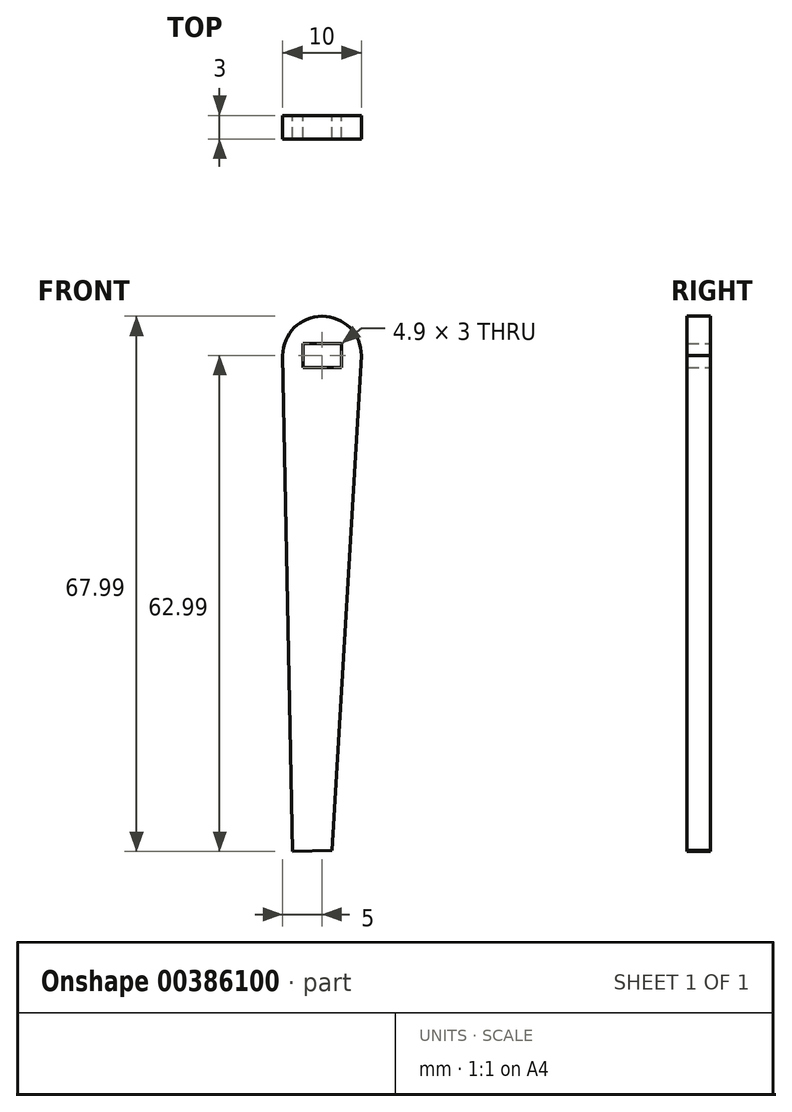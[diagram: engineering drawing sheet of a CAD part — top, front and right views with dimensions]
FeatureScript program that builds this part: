
annotation { "Feature Type Name" : "Feature", "Feature Type Description" : "" }
export const myFeature = defineFeature(function(context is Context, id is Id, definition is map)
    precondition{}
    {
        {
            var Q0;
            Q0=qCreatedBy(makeId("Front.planeOp"),FACE);
            var sketch = newSketch(context, id + "F0", { "sketchPlane" : qUnion([Q0])});
            skArc(sketch, "E0", {"start": v(5, 0) * mm, "mid": v(0, 5) * mm, "end": v(-5, 0) * mm});
            skLineSegment(sketch, "E1", {"start": v(-5, 0) * mm, "end": v(5, 0) * mm});
            skLineSegment(sketch, "E2", {"start": v(-5, 0) * mm, "end": v(-4.85, 1.2) * mm});
            skLineSegment(sketch, "E3", {"start": v(-5, 0) * mm, "end": v(-3.75, -62.99) * mm});
            skLineSegment(sketch, "E4", {"start": v(-3.75, -62.99) * mm, "end": v(1.25, -62.89) * mm});
            skLineSegment(sketch, "E5", {"start": v(1.25, -62.89) * mm, "end": v(5, 0) * mm});
            skSolve(sketch);
        }
        {
            var Q0;
            {var subQ0=sQuery(id+"F0.wireOp",EDGE,"E2");Q0=makeQuery(id+"F0.imprint","IMPRINT",FACE,{"disambiguationData":[TD([[makeQuery(id+"F0.imprint","IMPRINT",EDGE,{"derivedFrom":subQ0}),1.0]])]});}
            var Q1;
            {var subQ0=sQuery(id+"F0.wireOp",EDGE,"E1");Q1=makeQuery(id+"F0.imprint","IMPRINT",FACE,{"disambiguationData":[TD([[makeQuery(id+"F0.imprint","IMPRINT",EDGE,{"derivedFrom":subQ0}),1.0]])]});}
            var Q2;
            Q2=makeQuery(id+"F0.imprint","IMPRINT",FACE,{"disambiguationData":[TD([[makeQuery(id+"F0.imprint","IMPRINT",EDGE,{"derivedFrom":sQuery(id+"F0.wireOp",EDGE,"E1")}),-1.0]])]});
            extrude(context, id + "F1", {"entities" : qUnion([Q0, Q1, Q2]), "depth" : 3 * mm});
        }
        {
            var Q0;
            Q0=qCreatedBy(makeId("Front.planeOp"),FACE);
            var sketch = newSketch(context, id + "F2", { "sketchPlane" : qUnion([Q0])});
            skLineSegment(sketch, "E6.bottom", {"start": v(-2.45, -1.5) * mm, "end": v(2.45, -1.5) * mm});
            skLineSegment(sketch, "E6.top", {"start": v(-2.45, 1.5) * mm, "end": v(2.45, 1.5) * mm});
            skLineSegment(sketch, "E6.left", {"start": v(-2.45, -1.5) * mm, "end": v(-2.45, 1.5) * mm});
            skLineSegment(sketch, "E6.right", {"start": v(2.45, -1.5) * mm, "end": v(2.45, 1.5) * mm});
            skPoint(sketch, "E6.middle", {"position": v(0, 0) * mm});
            skSolve(sketch);
        }
        {
            var Q0;
            Q0 = qSketchRegion(id + "F2", true);
            extrude(context, id + "F3", {"entities" : qUnion([Q0]), "operationType" : NewBodyOperationType.REMOVE, "depth" : 25 * mm});
        }
    });
